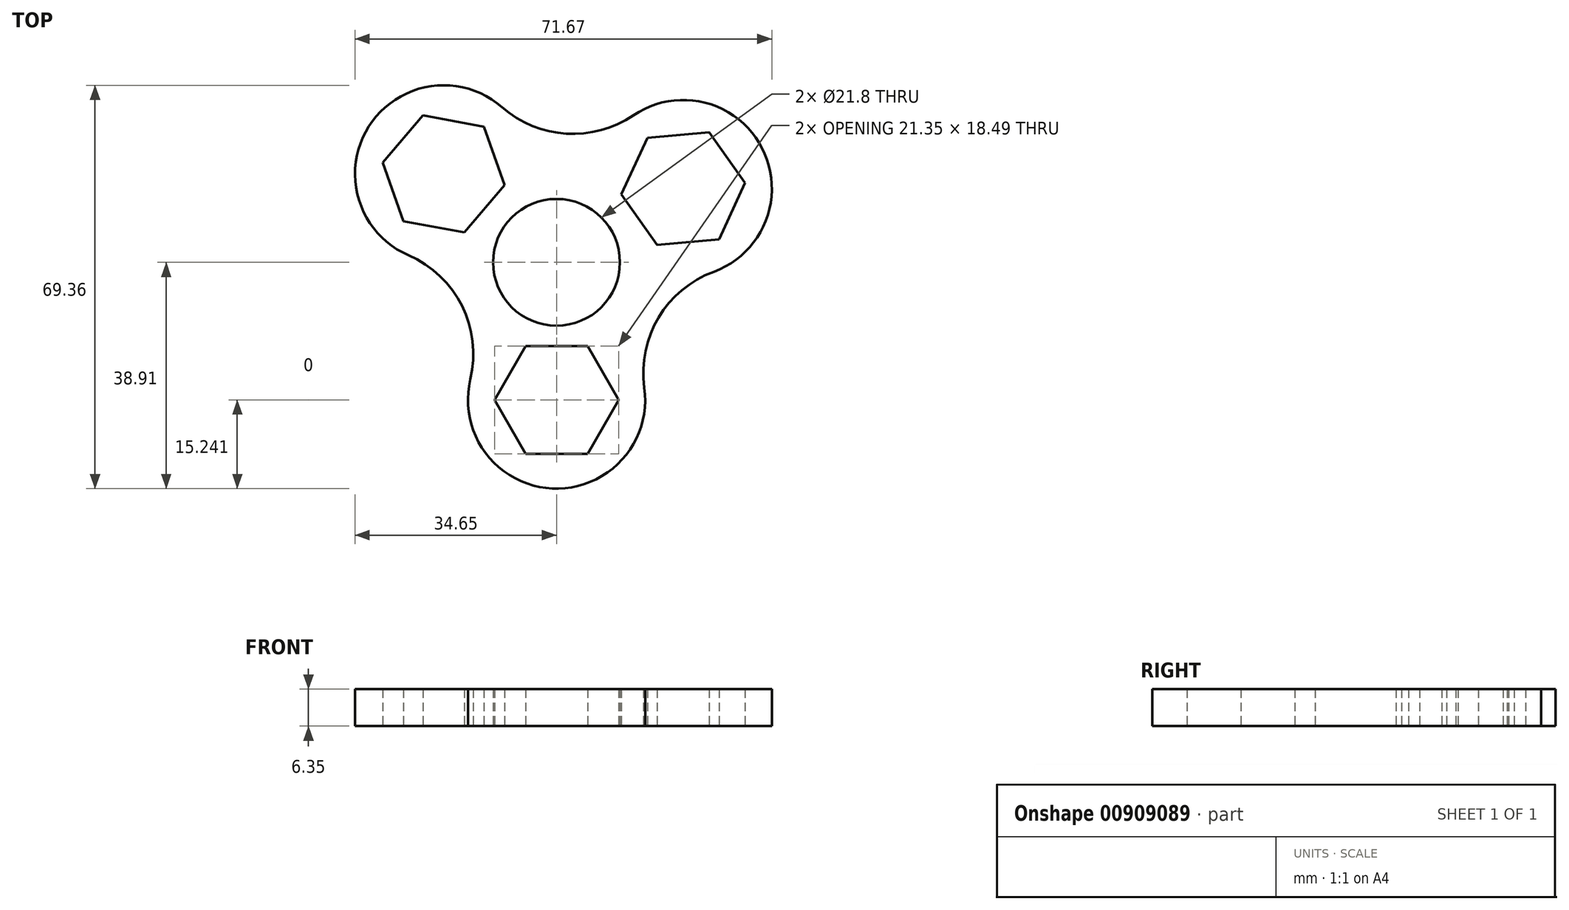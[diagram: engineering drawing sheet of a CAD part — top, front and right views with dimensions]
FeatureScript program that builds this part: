
annotation { "Feature Type Name" : "Feature", "Feature Type Description" : "" }
export const myFeature = defineFeature(function(context is Context, id is Id, definition is map)
    precondition{}
    {
        {
            var Q0;
            Q0=qCreatedBy(makeId("Top.planeOp"),FACE);
            var sketch = newSketch(context, id + "F0", { "sketchPlane" : qUnion([Q0])});
            skCircle(sketch, "E0", {"center": v(0, 0) * mm, "radius": 10.9 * mm});
            skCircle(sketch, "E1.cCircle", {"center": v(-19.4, 15.21) * mm, "radius": 9.25 * mm, "construction": true});
            skLineSegment(sketch, "E1.0", {"start": v(-8.9, 13.28) * mm, "end": v(-15.83, 5.15) * mm});
            skLineSegment(sketch, "E1.1", {"start": v(-15.83, 5.15) * mm, "end": v(-26.33, 7.08) * mm});
            skLineSegment(sketch, "E1.2", {"start": v(-26.33, 7.08) * mm, "end": v(-29.9, 17.14) * mm});
            skLineSegment(sketch, "E1.3", {"start": v(-29.9, 17.14) * mm, "end": v(-22.99, 25.27) * mm});
            skLineSegment(sketch, "E1.4", {"start": v(-22.99, 25.27) * mm, "end": v(-12.49, 23.34) * mm});
            skLineSegment(sketch, "E1.5", {"start": v(-12.49, 23.34) * mm, "end": v(-8.9, 13.28) * mm});
            skPoint(sketch, "E1.0.midPoint", {"position": v(-12.37, 9.22) * mm});
            skCircle(sketch, "E2.cCircle", {"center": v(21.78, 12.7) * mm, "radius": 9.25 * mm, "construction": true});
            skLineSegment(sketch, "E2.0", {"start": v(32.41, 13.68) * mm, "end": v(27.95, 3.98) * mm});
            skLineSegment(sketch, "E2.1", {"start": v(27.95, 3.98) * mm, "end": v(17.32, 3) * mm});
            skLineSegment(sketch, "E2.2", {"start": v(17.32, 3) * mm, "end": v(11.15, 11.7) * mm});
            skLineSegment(sketch, "E2.3", {"start": v(11.15, 11.7) * mm, "end": v(15.61, 21.4) * mm});
            skLineSegment(sketch, "E2.4", {"start": v(15.61, 21.4) * mm, "end": v(26.24, 22.4) * mm});
            skLineSegment(sketch, "E2.5", {"start": v(26.24, 22.4) * mm, "end": v(32.41, 13.68) * mm});
            skPoint(sketch, "E2.0.midPoint", {"position": v(30.18, 8.83) * mm});
            skCircle(sketch, "E3.cCircle", {"center": v(0, -23.67) * mm, "radius": 9.25 * mm, "construction": true});
            skLineSegment(sketch, "E3.0", {"start": v(5.34, -32.91) * mm, "end": v(-5.34, -32.91) * mm});
            skLineSegment(sketch, "E3.1", {"start": v(-5.34, -32.91) * mm, "end": v(-10.68, -23.67) * mm});
            skLineSegment(sketch, "E3.2", {"start": v(-10.68, -23.67) * mm, "end": v(-5.34, -14.42) * mm});
            skLineSegment(sketch, "E3.3", {"start": v(-5.34, -14.42) * mm, "end": v(5.34, -14.42) * mm});
            skLineSegment(sketch, "E3.4", {"start": v(5.34, -14.42) * mm, "end": v(10.68, -23.67) * mm});
            skLineSegment(sketch, "E3.5", {"start": v(10.68, -23.67) * mm, "end": v(5.34, -32.91) * mm});
            skPoint(sketch, "E3.0.midPoint", {"position": v(0, -32.91) * mm});
            skArc(sketch, "E4", {"start": v(-9.38, 26.69) * mm, "mid": v(-32.3, 23.35) * mm, "end": v(-25.47, 1.23) * mm});
            skArc(sketch, "E5", {"start": v(27.05, -1.6) * mm, "mid": v(35.34, 19.66) * mm, "end": v(13.23, 25.3) * mm});
            skArc(sketch, "E6", {"start": v(-14.82, -20.11) * mm, "mid": v(-0.74, -38.9) * mm, "end": v(15.1, -21.57) * mm});
            skArc(sketch, "E7", {"start": v(-14.82, -20.11) * mm, "mid": v(-16.26, -7.5) * mm, "end": v(-25.47, 1.23) * mm});
            skArc(sketch, "E8", {"start": v(-9.38, 26.69) * mm, "mid": v(1.69, 22.14) * mm, "end": v(13.23, 25.3) * mm});
            skArc(sketch, "E9", {"start": v(27.05, -1.6) * mm, "mid": v(17.55, -9.48) * mm, "end": v(15.1, -21.57) * mm});
            skSolve(sketch);
        }
        {
            var Q0;
            Q0 = qSketchRegion(id + "F0", true);
            extrude(context, id + "F1", {"entities" : qUnion([Q0]), "depth" : 6.35 * mm, "offsetDistance" : 25.4 * mm});
        }
    });
